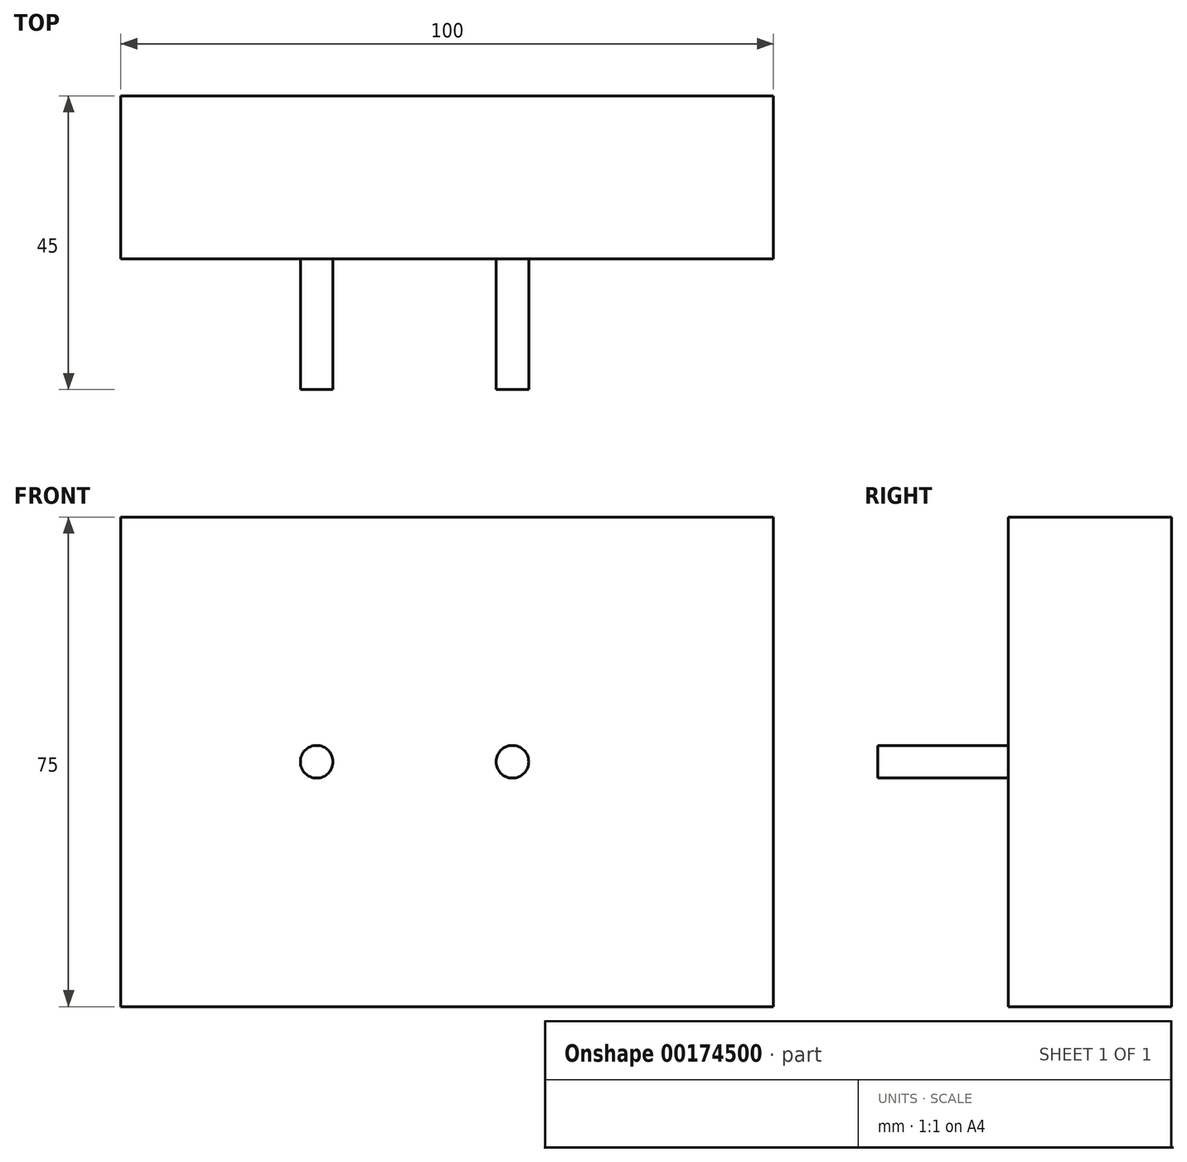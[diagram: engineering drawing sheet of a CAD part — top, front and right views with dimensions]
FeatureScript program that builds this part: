
annotation { "Feature Type Name" : "Feature", "Feature Type Description" : "" }
export const myFeature = defineFeature(function(context is Context, id is Id, definition is map)
    precondition{}
    {
        {
            var Q0;
            Q0=qCreatedBy(makeId("Front.planeOp"),FACE);
            var sketch = newSketch(context, id + "F0", { "sketchPlane" : qUnion([Q0])});
            skLineSegment(sketch, "E0.bottom", {"start": v(50, -37.5) * mm, "end": v(-50, -37.5) * mm});
            skLineSegment(sketch, "E0.top", {"start": v(50, 37.5) * mm, "end": v(-50, 37.5) * mm});
            skLineSegment(sketch, "E0.left", {"start": v(50, -37.5) * mm, "end": v(50, 37.5) * mm});
            skLineSegment(sketch, "E0.right", {"start": v(-50, -37.5) * mm, "end": v(-50, 37.5) * mm});
            skPoint(sketch, "E0.middle", {"position": v(0, 0) * mm});
            skSolve(sketch);
        }
        {
            var Q0;
            Q0 = qSketchRegion(id + "F0", true);
            extrude(context, id + "F1", {"entities" : qUnion([Q0]), "oppositeDirection" : true, "depth" : 25 * mm});
        }
        {
            var Q0;
            Q0=makeQuery(id+"F1.opExtrude","CAP_FACE",FACE,{"disambiguationData":[OSD([sQuery(id+"F0.wireOp",EDGE,"E0.bottom"),sQuery(id+"F0.wireOp",EDGE,"E0.top"),sQuery(id+"F0.wireOp",EDGE,"E0.left"),sQuery(id+"F0.wireOp",EDGE,"E0.right")])],"isStart":true});
            var sketch = newSketch(context, id + "F2", { "sketchPlane" : qUnion([Q0])});
            skCircle(sketch, "E1", {"center": v(10, 0) * mm, "radius": 2.5 * mm});
            skCircle(sketch, "E2", {"center": v(-20, 0) * mm, "radius": 2.5 * mm});
            skSolve(sketch);
        }
        {
            var Q0;
            Q0=makeQuery(id+"F2.imprint","IMPRINT",FACE,{"disambiguationData":[TD([[makeQuery(id+"F2.imprint","IMPRINT",EDGE,{"derivedFrom":sQuery(id+"F2.wireOp",EDGE,"E2")}),1.0]])]});
            var Q1;
            Q1=makeQuery(id+"F2.imprint","IMPRINT",FACE,{"disambiguationData":[TD([[makeQuery(id+"F2.imprint","IMPRINT",EDGE,{"derivedFrom":sQuery(id+"F2.wireOp",EDGE,"E1")}),1.0]])]});
            extrude(context, id + "F3", {"entities" : qUnion([Q0, Q1]), "operationType" : NewBodyOperationType.ADD, "depth" : 20 * mm});
        }
    });
